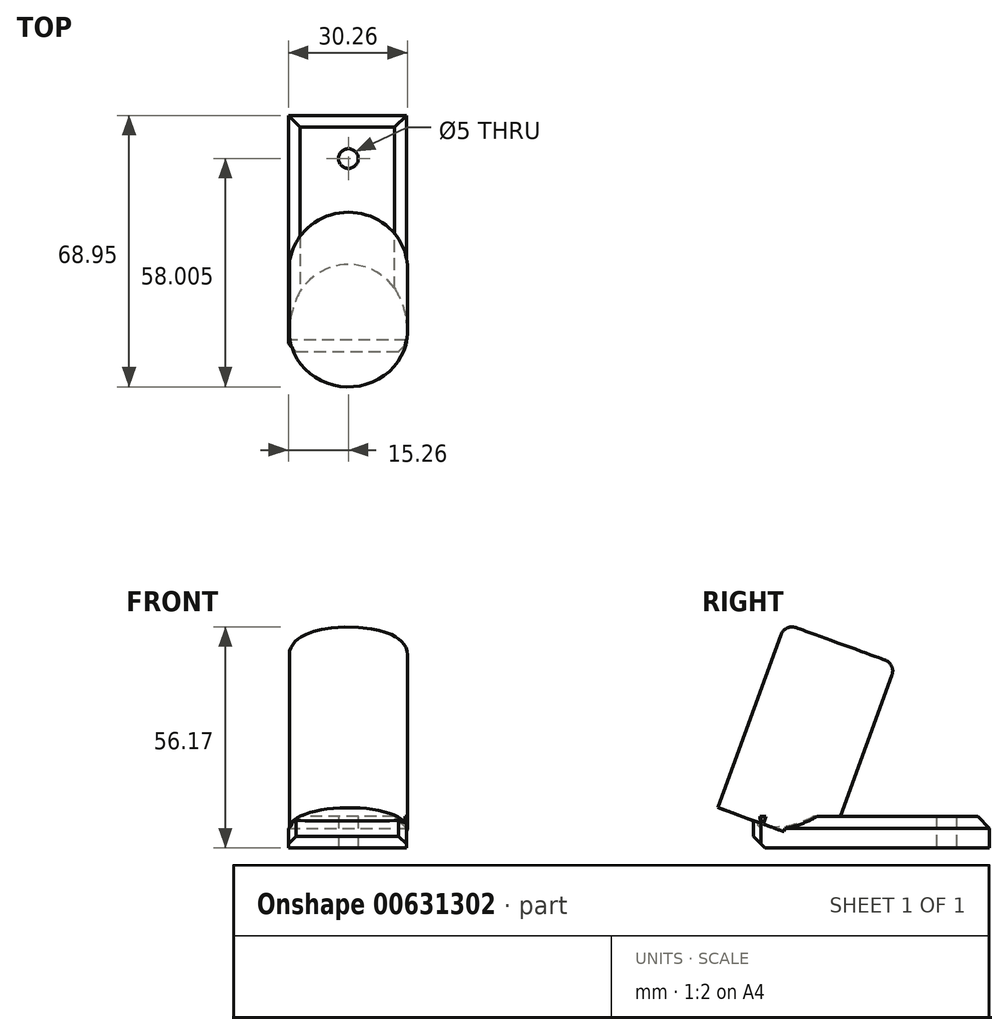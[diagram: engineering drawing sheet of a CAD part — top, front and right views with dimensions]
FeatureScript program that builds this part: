
annotation { "Feature Type Name" : "Feature", "Feature Type Description" : "" }
export const myFeature = defineFeature(function(context is Context, id is Id, definition is map)
    precondition{}
    {
        {
            var Q0;
            Q0=qCreatedBy(makeId("Top.planeOp"),FACE);
            var sketch = newSketch(context, id + "F0", { "sketchPlane" : qUnion([Q0])});
            skLineSegment(sketch, "E0.bottom", {"start": v(-15.26, 30) * mm, "end": v(14.74, 30) * mm});
            skLineSegment(sketch, "E0.top", {"start": v(-15.26, -30) * mm, "end": v(14.74, -30) * mm});
            skLineSegment(sketch, "E0.left", {"start": v(-15.26, 30) * mm, "end": v(-15.26, -30) * mm});
            skLineSegment(sketch, "E0.right", {"start": v(14.74, 30) * mm, "end": v(14.74, -30) * mm});
            skPoint(sketch, "E1.firstSnap0", {"position": v(-15.26, 0) * mm});
            skPoint(sketch, "E1.left.start.orphan", {"position": v(0, 0) * mm});
            skCircle(sketch, "E2", {"center": v(0, 19.05) * mm, "radius": 2.5 * mm});
            skSolve(sketch);
        }
        {
            var Q0;
            Q0=makeQuery(id+"F0.imprint","IMPRINT",FACE,{"disambiguationData":[TD([[makeQuery(id+"F0.imprint","IMPRINT",EDGE,{"derivedFrom":sQuery(id+"F0.wireOp",EDGE,"E0.bottom")}),-1.0]])]});
            extrude(context, id + "F1", {"entities" : qUnion([Q0]), "depth" : 8 * mm, "offsetDistance" : 25.4 * mm});
        }
        {
            var Q0;
            Q0=qCreatedBy(makeId("Right.planeOp"),FACE);
            var sketch = newSketch(context, id + "F2", { "sketchPlane" : qUnion([Q0])});
            skLineSegment(sketch, "E3", {"start": v(-10.76, 0) * mm, "end": v(6.26, 46.76) * mm});
            skLineSegment(sketch, "E4", {"start": v(6.26, 46.76) * mm, "end": v(-7.84, 51.89) * mm});
            skLineSegment(sketch, "E5", {"start": v(-7.84, 51.89) * mm, "end": v(-24.94, 4.9) * mm});
            skLineSegment(sketch, "E6", {"start": v(-24.94, 4.9) * mm, "end": v(-10.76, 0) * mm});
            skSolve(sketch);
        }
        {
            var Q0;
            Q0=makeQuery(id+"F2.imprint","IMPRINT",FACE,{"disambiguationData":[TD([[makeQuery(id+"F2.imprint","IMPRINT",EDGE,{"derivedFrom":sQuery(id+"F2.wireOp",EDGE,"E3")}),1.0]])]});
            var Q1;
            Q1=sQuery(id+"F2.wireOp",EDGE,"E5");
            revolve(context, id + "F3", {"operationType" : NewBodyOperationType.ADD, "surfaceOperationType" : NewSurfaceOperationType.NEW, "entities" : qUnion([Q0]), "axis" : qUnion([Q1]), "revolveType" : RevolveType.FULL});
        }
        {
            var Q0;
            Q0=makeQuery(id+"F1.opExtrude","CAP_EDGE",EDGE,{"disambiguationData":[OSD([sQuery(id+"F0.wireOp",EDGE,"E0.top")])],"isStart":true});
            var Q1;
            {var subQ0=sQuery(id+"F0.wireOp",EDGE,"E0.bottom");var subQ1=sQuery(id+"F0.wireOp",EDGE,"E0.right");Q1=makeQuery(id+"F3.boolean.opBoolean","SPLIT",EDGE,{"disambiguationData":[TD([makeQuery(id+"F1.opExtrude","SWEPT_FACE",FACE,{"disambiguationData":[OSD([subQ0])]})])],"derivedFrom":makeQuery(id+"F1.opExtrude","CAP_EDGE",EDGE,{"disambiguationData":[OSD([subQ1])],"isStart":false})});}
            var Q2;
            Q2=makeQuery(id+"F1.opExtrude","CAP_EDGE",EDGE,{"disambiguationData":[OSD([sQuery(id+"F0.wireOp",EDGE,"E0.left")])],"isStart":false});
            var Q3;
            Q3=makeQuery(id+"F1.opExtrude","CAP_EDGE",EDGE,{"disambiguationData":[OSD([sQuery(id+"F0.wireOp",EDGE,"E0.bottom")])],"isStart":false});
            chamfer(context, id + "F4", {"entities" : qUnion([Q0, Q1, Q2, Q3]), "width" : 3 * mm, "tangentPropagation" : true});
        }
        {
            var Q0;
            Q0=makeQuery(id+"F1.opExtrude","SWEPT_EDGE",EDGE,{"disambiguationData":[OSD([sQuery(id+"F0.wireOp",EDGE,"E0.top"),sQuery(id+"F0.wireOp",EDGE,"E0.left")])]});
            var Q1;
            Q1=makeQuery(id+"F1.opExtrude","SWEPT_EDGE",EDGE,{"disambiguationData":[OSD([sQuery(id+"F0.wireOp",EDGE,"E0.top"),sQuery(id+"F0.wireOp",EDGE,"E0.right")])]});
            chamfer(context, id + "F5", {"entities" : qUnion([Q0, Q1]), "width" : 2 * mm, "tangentPropagation" : true});
        }
        {
            var Q0;
            Q0=makeQuery(id+"F3.opRevolve","SWEPT_FACE",FACE,{"disambiguationData":[OSD([sQuery(id+"F2.wireOp",EDGE,"E4")])]});
            fillet(context, id + "F6", {"entities" : qUnion([Q0]), "radius" : 3 * mm, "tangentPropagation" : true, "allowEdgeOverflow" : false});
        }
    });
